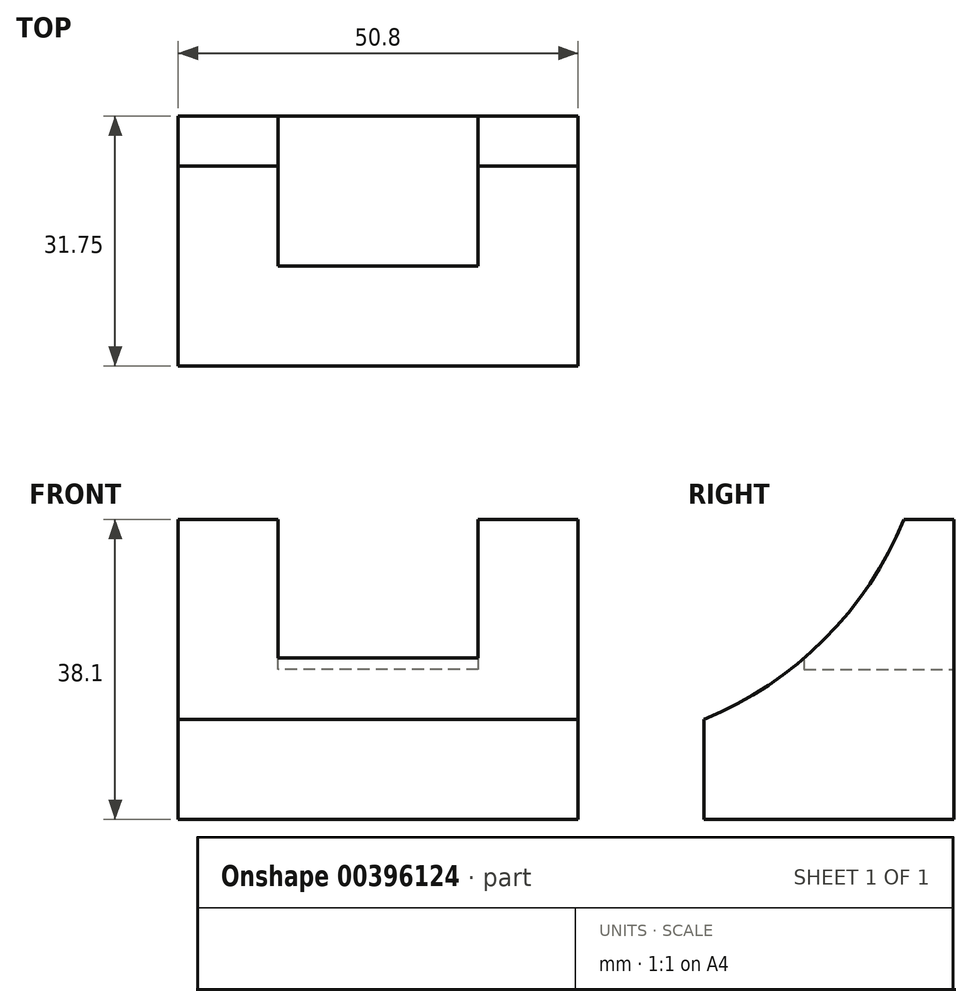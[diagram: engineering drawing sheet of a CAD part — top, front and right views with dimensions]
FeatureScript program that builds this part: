
annotation { "Feature Type Name" : "Feature", "Feature Type Description" : "" }
export const myFeature = defineFeature(function(context is Context, id is Id, definition is map)
    precondition{}
    {
        {
            var Q0;
            Q0=qCreatedBy(makeId("Right.planeOp"),FACE);
            var sketch = newSketch(context, id + "F0", { "sketchPlane" : qUnion([Q0])});
            skLineSegment(sketch, "E0", {"start": v(-26.39, 38.1) * mm, "end": v(-26.39, 0) * mm});
            skLineSegment(sketch, "E1", {"start": v(-26.39, 38.1) * mm, "end": v(5.36, 38.1) * mm});
            skLineSegment(sketch, "E2", {"start": v(5.36, 38.1) * mm, "end": v(5.36, 0) * mm});
            skLineSegment(sketch, "E3", {"start": v(5.36, 0) * mm, "end": v(-26.39, 0) * mm});
            skSolve(sketch);
        }
        {
            var Q0;
            Q0=makeQuery(id+"F0.imprint","IMPRINT",FACE,{"disambiguationData":[TD([[makeQuery(id+"F0.imprint","IMPRINT",EDGE,{"derivedFrom":sQuery(id+"F0.wireOp",EDGE,"E0")}),1.0]])]});
            extrude(context, id + "F1", {"entities" : qUnion([Q0]), "oppositeDirection" : true, "depth" : 50.8 * mm});
        }
        {
            var Q0;
            Q0=makeQuery(id+"F1.opExtrude","CAP_FACE",FACE,{"disambiguationData":[OSD([sQuery(id+"F0.wireOp",EDGE,"E0"),sQuery(id+"F0.wireOp",EDGE,"E1"),sQuery(id+"F0.wireOp",EDGE,"E2"),sQuery(id+"F0.wireOp",EDGE,"E3")])],"isStart":true});
            var sketch = newSketch(context, id + "F2", { "sketchPlane" : qUnion([Q0])});
            skArc(sketch, "E4", {"start": v(-26.39, 12.7) * mm, "mid": v(-11.14, 22.85) * mm, "end": v(-0.99, 38.1) * mm});
            skSolve(sketch);
        }
        {
            var Q0;
            {var subQ0=sQuery(id+"F2.wireOp",EDGE,"E4");Q0=makeQuery(id+"F2.imprint","IMPRINT",FACE,{"disambiguationData":[TD([[makeQuery(id+"F2.imprint","IMPRINT",EDGE,{"derivedFrom":subQ0}),1.0]])]});}
            extrude(context, id + "F3", {"entities" : qUnion([Q0]), "operationType" : NewBodyOperationType.REMOVE, "oppositeDirection" : true, "depth" : 50.8 * mm});
        }
        {
            var Q0;
            Q0=makeQuery(id+"F1.opExtrude","SWEPT_FACE",FACE,{"disambiguationData":[OSD([sQuery(id+"F0.wireOp",EDGE,"E2")])]});
            var sketch = newSketch(context, id + "F4", { "sketchPlane" : qUnion([Q0])});
            skLineSegment(sketch, "E5", {"start": v(12.7, 38.1) * mm, "end": v(12.7, 19.05) * mm});
            skLineSegment(sketch, "E6", {"start": v(12.7, 19.05) * mm, "end": v(38.1, 19.05) * mm});
            skLineSegment(sketch, "E7", {"start": v(38.1, 19.05) * mm, "end": v(38.1, 38.1) * mm});
            skSolve(sketch);
        }
        {
            var Q0;
            {var subQ0=sQuery(id+"F4.wireOp",EDGE,"E5");Q0=makeQuery(id+"F4.imprint","IMPRINT",FACE,{"disambiguationData":[TD([[makeQuery(id+"F4.imprint","IMPRINT",EDGE,{"derivedFrom":subQ0}),1.0]])]});}
            extrude(context, id + "F5", {"entities" : qUnion([Q0]), "operationType" : NewBodyOperationType.REMOVE, "oppositeDirection" : true, "depth" : 19.05 * mm});
        }
    });
